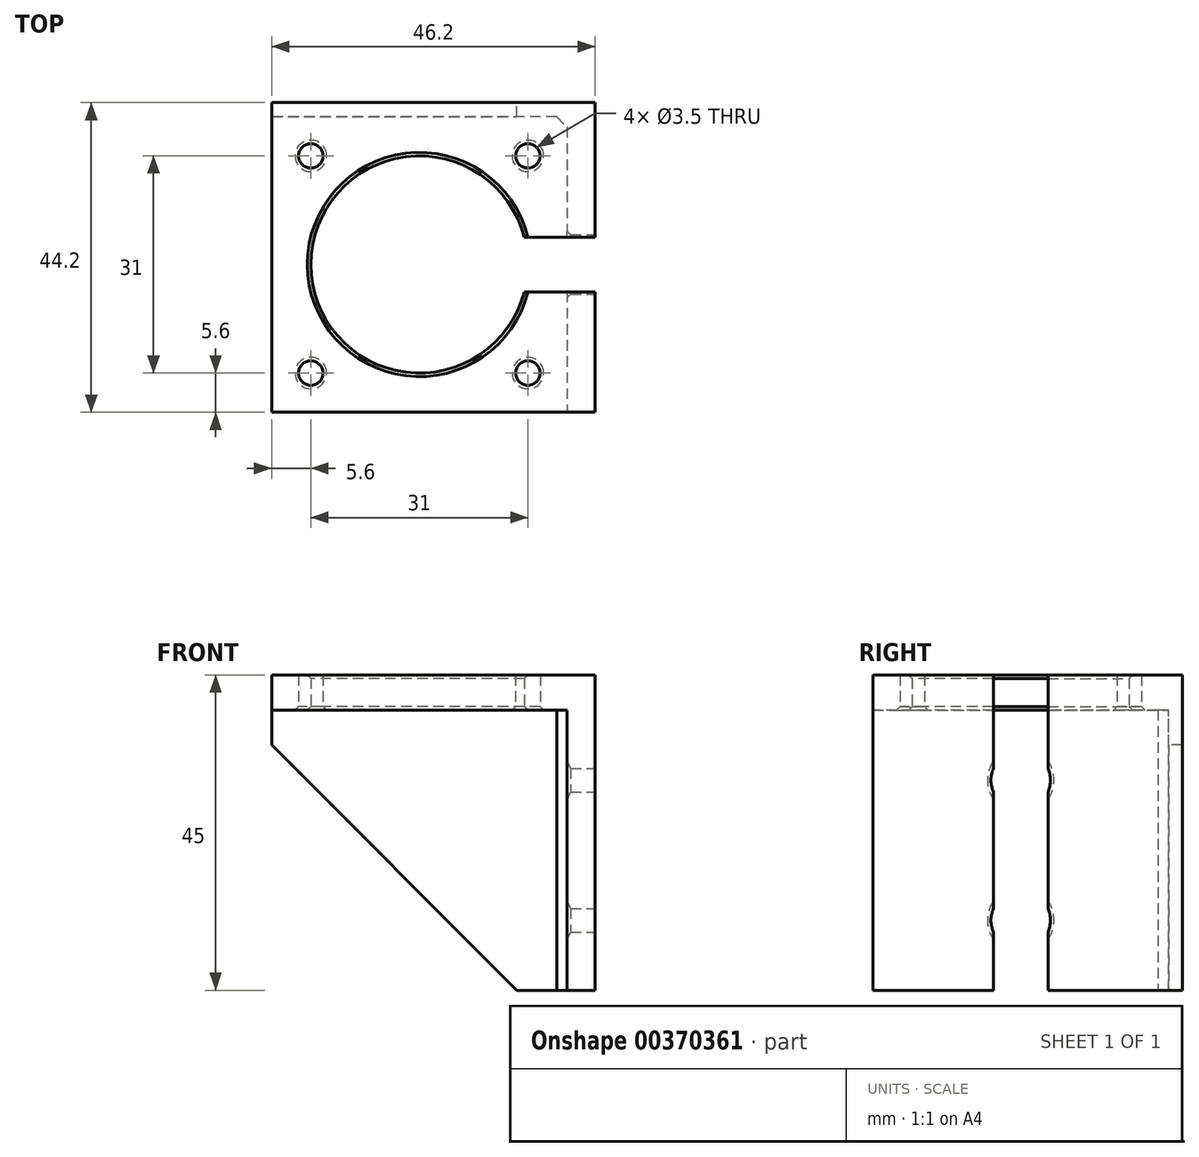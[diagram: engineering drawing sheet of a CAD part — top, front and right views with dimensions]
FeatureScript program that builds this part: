
annotation { "Feature Type Name" : "Feature", "Feature Type Description" : "" }
export const myFeature = defineFeature(function(context is Context, id is Id, definition is map)
    precondition{}
    {
        {
            var Q0;
            Q0=qCreatedBy(makeId("Top.planeOp"),FACE);
            var sketch = newSketch(context, id + "F0", { "sketchPlane" : qUnion([Q0])});
            skLineSegment(sketch, "E0.bottom", {"start": v(15.5, 15.5) * mm, "end": v(-15.5, 15.5) * mm});
            skLineSegment(sketch, "E0.top", {"start": v(15.5, -15.5) * mm, "end": v(-15.5, -15.5) * mm});
            skLineSegment(sketch, "E0.left", {"start": v(15.5, 15.5) * mm, "end": v(15.5, -15.5) * mm});
            skLineSegment(sketch, "E0.right", {"start": v(-15.5, 15.5) * mm, "end": v(-15.5, -15.5) * mm});
            skPoint(sketch, "E0.middle", {"position": v(0, 0) * mm});
            skLineSegment(sketch, "E1.bottom", {"start": v(21.1, 21.1) * mm, "end": v(-21.1, 21.1) * mm});
            skLineSegment(sketch, "E1.top", {"start": v(21.1, -21.1) * mm, "end": v(-21.1, -21.1) * mm});
            skLineSegment(sketch, "E1.left", {"start": v(21.1, 21.1) * mm, "end": v(21.1, -21.1) * mm});
            skLineSegment(sketch, "E1.right", {"start": v(-21.1, 21.1) * mm, "end": v(-21.1, -21.1) * mm});
            skCircle(sketch, "E2", {"center": v(-15.5, 15.5) * mm, "radius": 1.75 * mm});
            skCircle(sketch, "E3", {"center": v(-15.5, -15.5) * mm, "radius": 1.75 * mm});
            skCircle(sketch, "E4", {"center": v(15.5, -15.5) * mm, "radius": 1.75 * mm});
            skCircle(sketch, "E5", {"center": v(15.5, 15.5) * mm, "radius": 1.75 * mm});
            skLineSegment(sketch, "E6.bottom", {"start": v(-21.1, -21.1) * mm, "end": v(23.1, -21.1) * mm});
            skLineSegment(sketch, "E6.top", {"start": v(-21.1, 23.1) * mm, "end": v(23.1, 23.1) * mm});
            skLineSegment(sketch, "E6.left", {"start": v(-21.1, -21.1) * mm, "end": v(-21.1, 23.1) * mm});
            skLineSegment(sketch, "E6.right", {"start": v(23.1, -21.1) * mm, "end": v(23.1, 23.1) * mm});
            skCircle(sketch, "E7", {"center": v(0, 0) * mm, "radius": 15.5 * mm});
            skSolve(sketch);
        }
        {
            var Q0;
            Q0 = qSketchRegion(id + "F0", true);
            var Q1;
            {var subQ0=sQuery(id+"F0.wireOp",EDGE,"E7");var subQ1=sQuery(id+"F0.wireOp",EDGE,"E0.bottom");var subQ2=makeQuery(id+"F0.imprint","INTERSECT",VERTEX,{"derivedFrom":[subQ1,subQ0]});Q1=makeQuery(id+"F0.imprint","IMPRINT",FACE,{"disambiguationData":[TD([[makeQuery(id+"F0.imprint","IMPRINT",EDGE,{"disambiguationData":[TD([[subQ2,-1.0]])],"derivedFrom":subQ1}),1.0]])]});}
            var Q2;
            {var subQ0=sQuery(id+"F0.wireOp",EDGE,"E7");var subQ1=sQuery(id+"F0.wireOp",EDGE,"E0.top");var subQ2=makeQuery(id+"F0.imprint","INTERSECT",VERTEX,{"derivedFrom":[subQ1,subQ0]});Q2=makeQuery(id+"F0.imprint","IMPRINT",FACE,{"disambiguationData":[TD([[makeQuery(id+"F0.imprint","IMPRINT",EDGE,{"disambiguationData":[TD([[subQ2,-1.0]])],"derivedFrom":subQ1}),-1.0]])]});}
            var Q3;
            {var subQ0=sQuery(id+"F0.wireOp",EDGE,"E4");var subQ1=sQuery(id+"F0.wireOp",EDGE,"E0.top");var subQ2=makeQuery(id+"F0.imprint","INTERSECT",VERTEX,{"derivedFrom":[subQ1,subQ0]});Q3=makeQuery(id+"F0.imprint","IMPRINT",FACE,{"disambiguationData":[TD([[makeQuery(id+"F0.imprint","IMPRINT",EDGE,{"disambiguationData":[TD([[subQ2,-1.0]])],"derivedFrom":subQ1}),-1.0]])]});}
            var Q4;
            {var subQ0=sQuery(id+"F0.wireOp",EDGE,"E5");var subQ1=sQuery(id+"F0.wireOp",EDGE,"E0.bottom");var subQ2=makeQuery(id+"F0.imprint","INTERSECT",VERTEX,{"derivedFrom":[subQ1,subQ0]});Q4=makeQuery(id+"F0.imprint","IMPRINT",FACE,{"disambiguationData":[TD([[makeQuery(id+"F0.imprint","IMPRINT",EDGE,{"disambiguationData":[TD([[subQ2,-1.0]])],"derivedFrom":subQ1}),1.0]])]});}
            extrude(context, id + "F1", {"entities" : qUnion([Q0, Q1, Q2, Q3, Q4]), "depth" : 5 * mm});
        }
        {
            var Q0;
            {var subQ4=sQuery(id+"F0.wireOp",EDGE,"E1.bottom");Q0=makeQuery(id+"F0.imprint","IMPRINT",FACE,{"disambiguationData":[TD([[makeQuery(id+"F0.imprint","IMPRINT",EDGE,{"derivedFrom":subQ4}),-1.0]])]});}
            extrude(context, id + "F2", {"entities" : qUnion([Q0]), "operationType" : NewBodyOperationType.ADD, "oppositeDirection" : true, "depth" : 40 * mm});
        }
        {
            var Q0;
            {var subQ0=sQuery(id+"F0.wireOp",EDGE,"E6.right");Q0=makeQuery(id+"F2.boolean.opBoolean","MERGE",FACE,{"derivedFrom":[makeQuery(id+"F1.opExtrude","SWEPT_FACE",FACE,{"disambiguationData":[OSD([subQ0])]}),makeQuery(id+"F2.opExtrude","SWEPT_FACE",FACE,{"disambiguationData":[OSD([subQ0])]})]});}
            extrude(context, id + "F3", {"entities" : qUnion([Q0]), "operationType" : NewBodyOperationType.ADD, "depth" : 2 * mm});
        }
        {
            var Q0;
            Q0=makeQuery(id+"F3.opExtrude","CAP_FACE",FACE,{"disambiguationData":[OSD([sQuery(id+"F0.wireOp",EDGE,"E6.right")])],"isStart":false});
            var sketch = newSketch(context, id + "F4", { "sketchPlane" : qUnion([Q0])});
            skLineSegment(sketch, "E8", {"start": v(0, 0) * mm, "end": v(0, -10) * mm});
            skCircle(sketch, "E9", {"center": v(0, -10) * mm, "radius": 4.25 * mm});
            skLineSegment(sketch, "E10", {"start": v(0, -10) * mm, "end": v(0, -30) * mm});
            skCircle(sketch, "E11", {"center": v(0, -30) * mm, "radius": 4.25 * mm});
            skLineSegment(sketch, "E12.top", {"start": v(-4.25, -30) * mm, "end": v(4.25, -30) * mm});
            skLineSegment(sketch, "E13.bottom", {"start": v(3.9, -16.75) * mm, "end": v(-3.9, -16.75) * mm});
            skLineSegment(sketch, "E13.top", {"start": v(3.9, -23.25) * mm, "end": v(-3.9, -23.25) * mm});
            skLineSegment(sketch, "E13.left", {"start": v(3.9, -16.75) * mm, "end": v(3.9, -23.25) * mm});
            skLineSegment(sketch, "E13.right", {"start": v(-3.9, -16.75) * mm, "end": v(-3.9, -23.25) * mm});
            skPoint(sketch, "E13.middle", {"position": v(0, -20) * mm});
            skLineSegment(sketch, "E14", {"start": v(0, -10) * mm, "end": v(0, -40) * mm});
            skLineSegment(sketch, "E15", {"start": v(0, 0) * mm, "end": v(-21.1, 0) * mm});
            skSolve(sketch);
        }
        {
            var Q0;
            {var subQ0=sQuery(id+"F4.wireOp",EDGE,"E10");var subQ1=sQuery(id+"F4.wireOp",EDGE,"E8");var subQ2=makeQuery(id+"F4.imprint","INTERSECT",VERTEX,{"derivedFrom":[subQ1,subQ0]});Q0=makeQuery(id+"F4.imprint","IMPRINT",FACE,{"disambiguationData":[TD([[makeQuery(id+"F4.imprint","IMPRINT",EDGE,{"disambiguationData":[TD([[subQ2,1.0]])],"derivedFrom":subQ1}),1.0]])]});}
            var Q1;
            {var subQ0=sQuery(id+"F4.wireOp",EDGE,"E9");var subQ1=sQuery(id+"F4.wireOp",EDGE,"E8");var subQ2=makeQuery(id+"F4.imprint","INTERSECT",VERTEX,{"derivedFrom":[subQ1,subQ0]});Q1=makeQuery(id+"F4.imprint","IMPRINT",FACE,{"disambiguationData":[TD([[makeQuery(id+"F4.imprint","IMPRINT",EDGE,{"disambiguationData":[TD([[subQ2,-1.0]])],"derivedFrom":subQ1}),1.0]])]});}
            var Q2;
            {var subQ0=sQuery(id+"F4.wireOp",EDGE,"E9");var subQ1=sQuery(id+"F4.wireOp",EDGE,"E8");var subQ2=makeQuery(id+"F4.imprint","INTERSECT",VERTEX,{"derivedFrom":[subQ1,subQ0]});Q2=makeQuery(id+"F4.imprint","IMPRINT",FACE,{"disambiguationData":[TD([[makeQuery(id+"F4.imprint","IMPRINT",EDGE,{"disambiguationData":[TD([[subQ2,-1.0]])],"derivedFrom":subQ1}),-1.0]])]});}
            var Q3;
            {var subQ4=sQuery(id+"F4.wireOp",EDGE,"E8");var subQ6=sQuery(id+"F4.wireOp",EDGE,"E10");var subQ7=makeQuery(id+"F4.imprint","INTERSECT",VERTEX,{"derivedFrom":[subQ4,subQ6]});Q3=makeQuery(id+"F4.imprint","IMPRINT",FACE,{"disambiguationData":[TD([[makeQuery(id+"F4.imprint","IMPRINT",EDGE,{"disambiguationData":[TD([[subQ7,1.0]])],"derivedFrom":subQ4}),-1.0]])]});}
            var Q4;
            {var subQ1=sQuery(id+"F4.wireOp",EDGE,"rvTly6eO-xJPG-WOcs-rglb-mu07cQ64ZAQ2");var subQ3=sQuery(id+"F4.wireOp",EDGE,"E11");var subQ4=makeQuery(id+"F4.imprint","INTERSECT",VERTEX,{"derivedFrom":[subQ1,subQ3]});Q4=makeQuery(id+"F4.imprint","IMPRINT",FACE,{"disambiguationData":[TD([[makeQuery(id+"F4.imprint","IMPRINT",EDGE,{"disambiguationData":[TD([[subQ4,1.0]])],"derivedFrom":subQ3}),1.0]])]});}
            var Q5;
            {var subQ1=sQuery(id+"F4.wireOp",EDGE,"rvTly6eO-xJPG-WOcs-rglb-mu07cQ64ZAQ2");var subQ3=sQuery(id+"F4.wireOp",EDGE,"E11");var subQ4=makeQuery(id+"F4.imprint","INTERSECT",VERTEX,{"derivedFrom":[subQ1,subQ3]});Q5=makeQuery(id+"F4.imprint","IMPRINT",FACE,{"disambiguationData":[TD([[makeQuery(id+"F4.imprint","IMPRINT",EDGE,{"disambiguationData":[TD([[subQ4,1.0]])],"derivedFrom":subQ1}),1.0]])]});}
            var Q6;
            {var subQ0=sQuery(id+"F4.wireOp",EDGE,"E12.top");var subQ1=sQuery(id+"F4.wireOp",EDGE,"E10");var subQ2=makeQuery(id+"F4.imprint","INTERSECT",VERTEX,{"derivedFrom":[sQuery(id+"F4.wireOp",EDGE,"rvTly6eO-xJPG-WOcs-rglb-mu07cQ64ZAQ2"),subQ1,subQ0]});Q6=makeQuery(id+"F4.imprint","IMPRINT",FACE,{"disambiguationData":[TD([[makeQuery(id+"F4.imprint","IMPRINT",EDGE,{"disambiguationData":[TD([[subQ2,1.0]])],"derivedFrom":subQ1}),1.0]])]});}
            var Q7;
            {var subQ0=sQuery(id+"F4.wireOp",EDGE,"E12.top");var subQ5=sQuery(id+"F4.wireOp",EDGE,"E12.left");var subQ7=makeQuery(id+"F4.imprint","INTERSECT",VERTEX,{"derivedFrom":[subQ0,subQ5]});Q7=makeQuery(id+"F4.imprint","IMPRINT",FACE,{"disambiguationData":[TD([[makeQuery(id+"F4.imprint","IMPRINT",EDGE,{"disambiguationData":[TD([[subQ7,1.0]])],"derivedFrom":subQ5}),1.0]])]});}
            var Q8;
            {var subQ0=sQuery(id+"F4.wireOp",EDGE,"E12.top");var subQ1=sQuery(id+"F4.wireOp",EDGE,"E11");var subQ2=makeQuery(id+"F4.imprint","INTERSECT",VERTEX,{"derivedFrom":[subQ1,subQ0]});Q8=makeQuery(id+"F4.imprint","IMPRINT",FACE,{"disambiguationData":[TD([[makeQuery(id+"F4.imprint","IMPRINT",EDGE,{"disambiguationData":[TD([[subQ2,1.0]])],"derivedFrom":subQ0}),1.0]])]});}
            extrude(context, id + "F5", {"entities" : qUnion([Q0, Q1, Q2, Q3, Q4, Q5, Q6, Q7, Q8]), "operationType" : NewBodyOperationType.REMOVE, "oppositeDirection" : true, "depth" : 25 * mm});
        }
        {
            var Q0;
            {var subQ5=sQuery(id+"F4.wireOp",EDGE,"E13.left");Q0=makeQuery(id+"F4.imprint","IMPRINT",FACE,{"disambiguationData":[TD([[makeQuery(id+"F4.imprint","IMPRINT",EDGE,{"derivedFrom":subQ5}),-1.0]])]});}
            var Q1;
            {var subQ5=sQuery(id+"F4.wireOp",EDGE,"E13.right");Q1=makeQuery(id+"F4.imprint","IMPRINT",FACE,{"disambiguationData":[TD([[makeQuery(id+"F4.imprint","IMPRINT",EDGE,{"derivedFrom":subQ5}),1.0]])]});}
            extrude(context, id + "F6", {"entities" : qUnion([Q0, Q1]), "operationType" : NewBodyOperationType.ADD, "depth" : 2 * mm});
        }
        {
            var Q0;
            Q0=makeQuery(id+"F5.boolean.opBoolean","INTERSECT",EDGE,{"derivedFrom":[makeQuery(id+"F2.opExtrude","SWEPT_FACE",FACE,{"disambiguationData":[OSD([sQuery(id+"F0.wireOp",EDGE,"E1.left")])]}),makeQuery(id+"F5.opExtrude","SWEPT_FACE",FACE,{"disambiguationData":[OSD([sQuery(id+"F4.wireOp",EDGE,"E11")])]})]});
            var Q1;
            Q1=makeQuery(id+"F5.boolean.opBoolean","INTERSECT",EDGE,{"derivedFrom":[makeQuery(id+"F2.opExtrude","SWEPT_FACE",FACE,{"disambiguationData":[OSD([sQuery(id+"F0.wireOp",EDGE,"E1.left")])]}),makeQuery(id+"F5.opExtrude","SWEPT_FACE",FACE,{"disambiguationData":[OSD([sQuery(id+"F4.wireOp",EDGE,"E9")])]})]});
            var Q2;
            Q2=makeQuery(id+"F1.opExtrude","CAP_EDGE",EDGE,{"disambiguationData":[OSD([sQuery(id+"F0.wireOp",EDGE,"E7")])],"isStart":false});
            var Q3;
            Q3=makeQuery(id+"F1.opExtrude","CAP_EDGE",EDGE,{"disambiguationData":[OSD([sQuery(id+"F0.wireOp",EDGE,"E7")])],"isStart":true});
            var Q4;
            Q4=makeQuery(id+"F1.opExtrude","CAP_EDGE",EDGE,{"disambiguationData":[OSD([sQuery(id+"F0.wireOp",EDGE,"E2")])],"isStart":true});
            var Q5;
            Q5=makeQuery(id+"F1.opExtrude","CAP_EDGE",EDGE,{"disambiguationData":[OSD([sQuery(id+"F0.wireOp",EDGE,"E3")])],"isStart":true});
            var Q6;
            Q6=makeQuery(id+"F1.opExtrude","CAP_EDGE",EDGE,{"disambiguationData":[OSD([sQuery(id+"F0.wireOp",EDGE,"E4")])],"isStart":true});
            var Q7;
            Q7=makeQuery(id+"F1.opExtrude","CAP_EDGE",EDGE,{"disambiguationData":[OSD([sQuery(id+"F0.wireOp",EDGE,"E5")])],"isStart":true});
            chamfer(context, id + "F7", {"entities" : qUnion([Q0, Q1, Q2, Q3, Q4, Q5, Q6, Q7]), "width" : .5 * mm, "tangentPropagation" : true});
        }
        {
            var Q0;
            Q0=makeQuery(id+"F2.opExtrude","CAP_EDGE",EDGE,{"disambiguationData":[OSD([sQuery(id+"F0.wireOp",EDGE,"E6.left")])],"isStart":false});
            chamfer(context, id + "F8", {"entities" : qUnion([Q0]), "width" : 35 * mm, "tangentPropagation" : true});
        }
        {
            var Q0;
            Q0=makeQuery(id+"F6.opExtrude","SWEPT_FACE",FACE,{"disambiguationData":[OSD([sQuery(id+"F4.wireOp",EDGE,"E13.top")])]});
            extrude(context, id + "F9", {"entities" : qUnion([Q0]), "operationType" : NewBodyOperationType.ADD, "depth" : 16.75 * mm});
        }
        {
            var Q0;
            Q0=makeQuery(id+"F6.opExtrude","SWEPT_FACE",FACE,{"disambiguationData":[OSD([sQuery(id+"F4.wireOp",EDGE,"E13.bottom")])]});
            extrude(context, id + "F10", {"entities" : qUnion([Q0]), "operationType" : NewBodyOperationType.ADD, "depth" : 21.75 * mm});
        }
        {
            var Q0;
            {var subQ2=sQuery(id+"F4.wireOp",EDGE,"E13.bottom");var subQ4=makeQuery(id+"F6.opExtrude","CAP_EDGE",EDGE,{"disambiguationData":[OSD([subQ2])],"isStart":true});Q0=makeQuery(id+"F10.opExtrude","SWEPT_FACE",FACE,{"disambiguationData":[OSD([subQ2]),TDD([makeQuery(id+"F6.boolean.opBoolean","SPLIT",EDGE,{"disambiguationData":[TD([makeQuery(id+"F6.opExtrude","SWEPT_FACE",FACE,{"disambiguationData":[OSD([sQuery(id+"F4.wireOp",EDGE,"E13.left")])]})])],"derivedFrom":subQ4}),makeQuery(id+"F6.boolean.opBoolean","SPLIT",EDGE,{"disambiguationData":[TD([makeQuery(id+"F6.opExtrude","SWEPT_FACE",FACE,{"disambiguationData":[OSD([sQuery(id+"F4.wireOp",EDGE,"E13.right")])]})])],"derivedFrom":subQ4})])]});}
            var Q1;
            {var subQ2=sQuery(id+"F4.wireOp",EDGE,"E13.top");var subQ4=makeQuery(id+"F6.opExtrude","CAP_EDGE",EDGE,{"disambiguationData":[OSD([subQ2])],"isStart":true});Q1=makeQuery(id+"F9.opExtrude","SWEPT_FACE",FACE,{"disambiguationData":[OSD([subQ2]),TDD([makeQuery(id+"F6.boolean.opBoolean","SPLIT",EDGE,{"disambiguationData":[TD([makeQuery(id+"F6.opExtrude","SWEPT_FACE",FACE,{"disambiguationData":[OSD([sQuery(id+"F4.wireOp",EDGE,"E13.left")])]})])],"derivedFrom":subQ4}),makeQuery(id+"F6.boolean.opBoolean","SPLIT",EDGE,{"disambiguationData":[TD([makeQuery(id+"F6.opExtrude","SWEPT_FACE",FACE,{"disambiguationData":[OSD([sQuery(id+"F4.wireOp",EDGE,"E13.right")])]})])],"derivedFrom":subQ4})])]});}
            extrude(context, id + "F11", {"entities" : qUnion([Q0, Q1]), "operationType" : NewBodyOperationType.REMOVE, "oppositeDirection" : true, "depth" : 25 * mm});
        }
        {
            var Q0;
            Q0=makeQuery(id+"F2.opExtrude","CAP_EDGE",EDGE,{"disambiguationData":[OSD([sQuery(id+"F0.wireOp",EDGE,"E1.left")])],"isStart":true});
            var Q1;
            Q1=makeQuery(id+"F2.opExtrude","SWEPT_EDGE",EDGE,{"disambiguationData":[OSD([sQuery(id+"F0.wireOp",EDGE,"E1.bottom"),sQuery(id+"F0.wireOp",EDGE,"E1.left")])]});
            var Q2;
            Q2=makeQuery(id+"F2.opExtrude","CAP_EDGE",EDGE,{"disambiguationData":[OSD([sQuery(id+"F0.wireOp",EDGE,"E1.bottom")])],"isStart":true});
            chamfer(context, id + "F12", {"entities" : qUnion([Q0, Q1, Q2]), "width" : 1.5 * mm, "tangentPropagation" : true});
        }
    });
